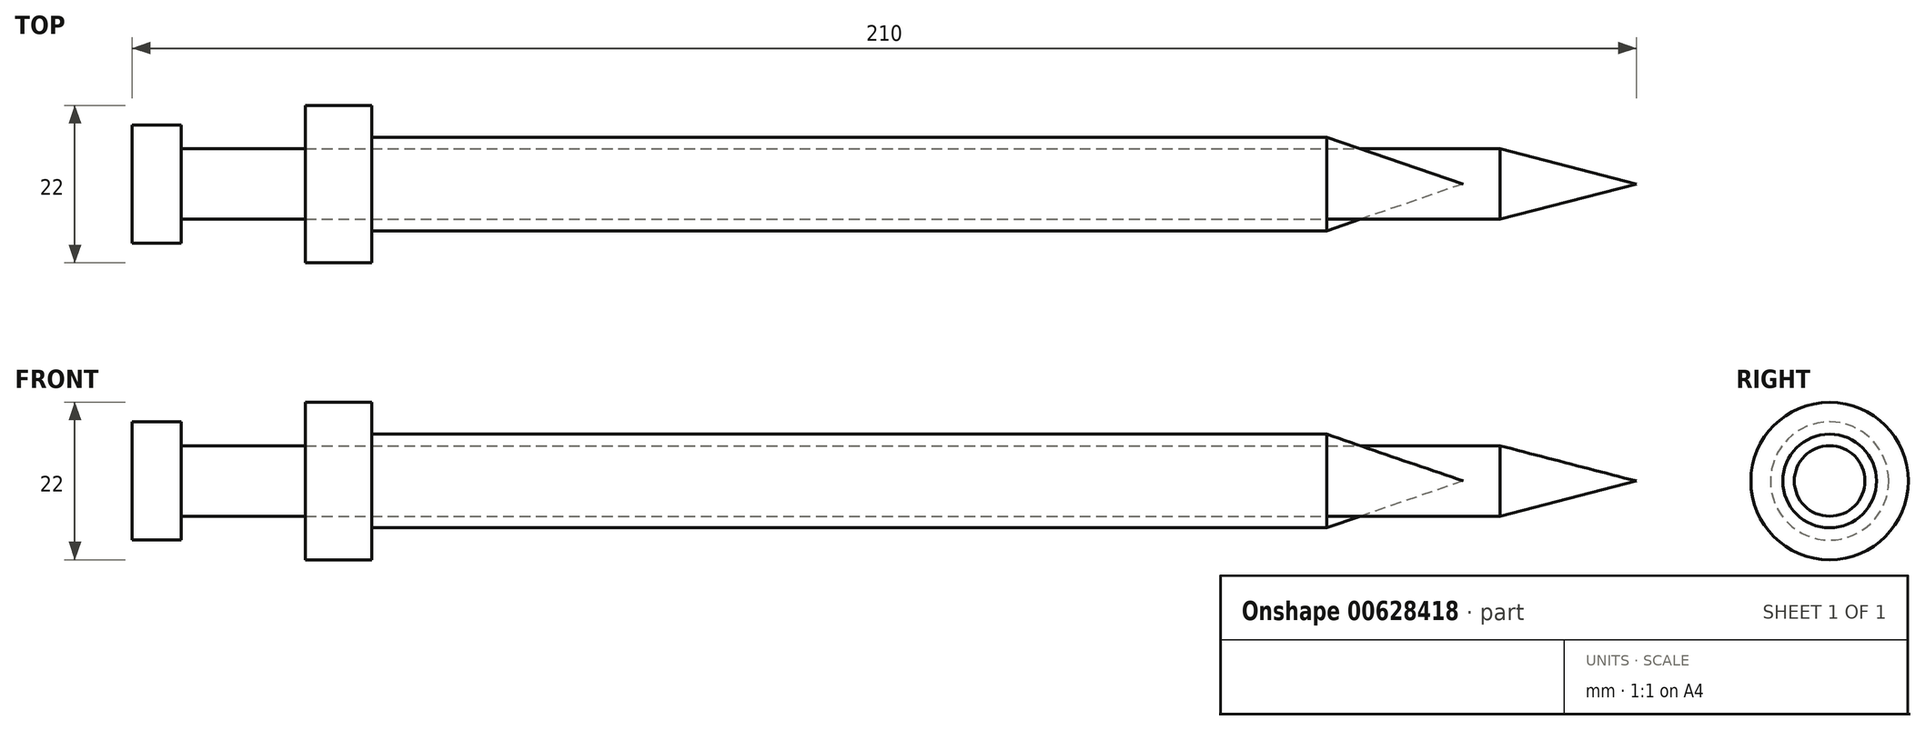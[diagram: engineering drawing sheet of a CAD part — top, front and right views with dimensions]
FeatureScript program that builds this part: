
annotation { "Feature Type Name" : "Feature", "Feature Type Description" : "" }
export const myFeature = defineFeature(function(context is Context, id is Id, definition is map)
    precondition{}
    {
        {
            var Q0;
            Q0=qCreatedBy(makeId("Front.planeOp"),FACE);
            var sketch = newSketch(context, id + "F0", { "sketchPlane" : qUnion([Q0])});
            skLineSegment(sketch, "E0", {"start": v(-105, 0) * mm, "end": v(-105, 8.26) * mm});
            skLineSegment(sketch, "E1", {"start": v(-105, 8.26) * mm, "end": v(-98.2, 8.26) * mm});
            skLineSegment(sketch, "E2", {"start": v(-98.2, 8.26) * mm, "end": v(-98.2, 4.93) * mm});
            skLineSegment(sketch, "E3", {"start": v(105, 0) * mm, "end": v(-105, 0) * mm});
            skLineSegment(sketch, "E4", {"start": v(105, 0) * mm, "end": v(85.95, 4.93) * mm});
            skLineSegment(sketch, "E5", {"start": v(-98.2, 4.93) * mm, "end": v(85.95, 4.93) * mm});
            skSolve(sketch);
        }
        {
            var Q0;
            Q0 = qSketchRegion(id + "F0", true);
            var Q1;
            Q1=sQuery(id+"F0.wireOp",EDGE,"E3");
            revolve(context, id + "F1", {"entities" : qUnion([Q0]), "axis" : qUnion([Q1]), "revolveType" : RevolveType.FULL});
        }
        {
            var Q0;
            Q0=qCreatedBy(makeId("Front.planeOp"),FACE);
            var sketch = newSketch(context, id + "F2", { "sketchPlane" : qUnion([Q0])});
            skLineSegment(sketch, "E6", {"start": v(-80.82, 0) * mm, "end": v(-80.82, 11) * mm});
            skLineSegment(sketch, "E7", {"start": v(-80.82, 11) * mm, "end": v(-71.58, 11) * mm});
            skLineSegment(sketch, "E8", {"start": v(-71.58, 11) * mm, "end": v(-71.58, 6.54) * mm});
            skLineSegment(sketch, "E9", {"start": v(-71.58, 6.54) * mm, "end": v(61.77, 6.54) * mm});
            skLineSegment(sketch, "E10", {"start": v(61.77, 6.54) * mm, "end": v(80.82, 0) * mm});
            skLineSegment(sketch, "E11", {"start": v(80.82, 0) * mm, "end": v(-80.82, 0) * mm});
            skSolve(sketch);
        }
        {
            var Q0;
            Q0 = qSketchRegion(id + "F2", true);
            var Q1;
            Q1=sQuery(id+"F2.wireOp",EDGE,"E11");
            revolve(context, id + "F3", {"entities" : qUnion([Q0]), "axis" : qUnion([Q1]), "revolveType" : RevolveType.FULL});
        }
    });
